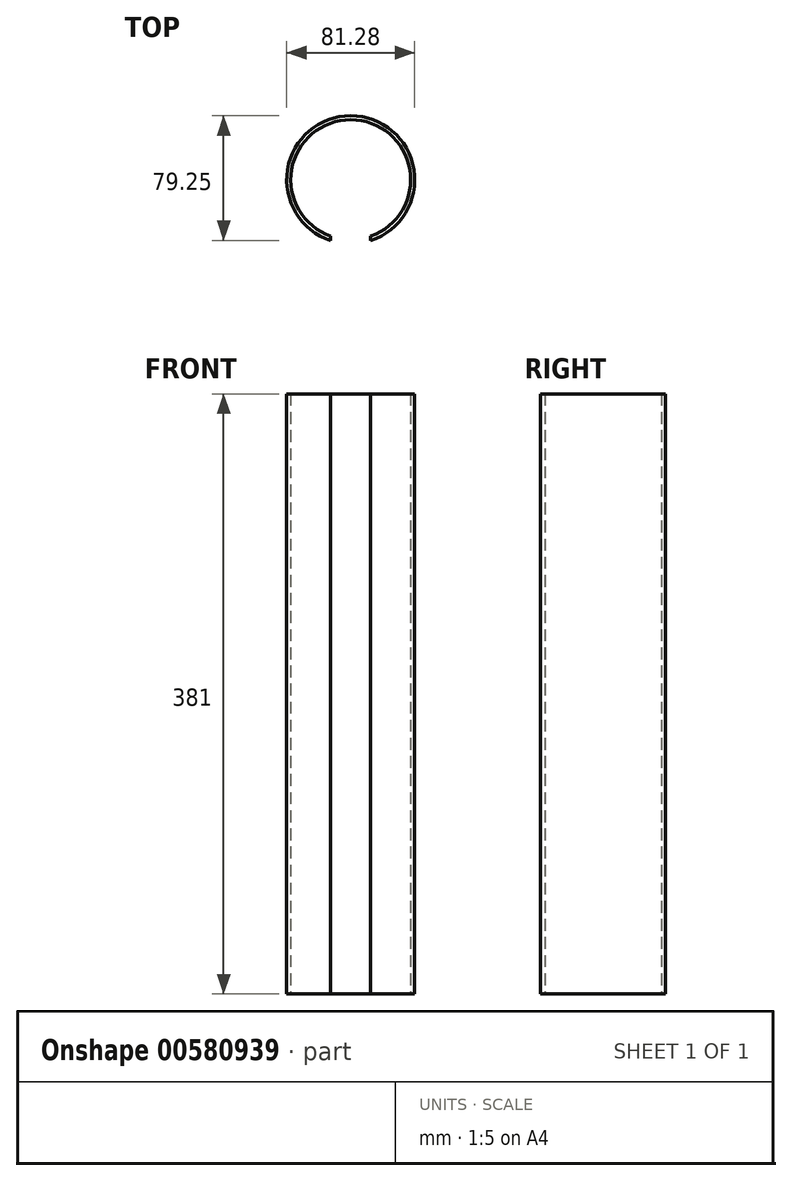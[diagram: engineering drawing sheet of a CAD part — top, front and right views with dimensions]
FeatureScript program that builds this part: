
annotation { "Feature Type Name" : "Feature", "Feature Type Description" : "" }
export const myFeature = defineFeature(function(context is Context, id is Id, definition is map)
    precondition{}
    {
        {
            var Q0;
            Q0=qCreatedBy(makeId("Top.planeOp"),FACE);
            var sketch = newSketch(context, id + "F0", { "sketchPlane" : qUnion([Q0])});
            skArc(sketch, "E0", {"start": v(8.75, -20.74) * mm, "mid": v(-3.95, 58.5) * mm, "end": v(-16.65, -20.74) * mm});
            skArc(sketch, "E1", {"start": v(8.75, -18.06) * mm, "mid": v(-3.95, 55.97) * mm, "end": v(-16.65, -18.06) * mm});
            skLineSegment(sketch, "E2", {"start": v(-16.65, -20.74) * mm, "end": v(-16.65, -18.06) * mm});
            skLineSegment(sketch, "E3", {"start": v(8.75, -20.74) * mm, "end": v(8.75, -18.06) * mm});
            skSolve(sketch);
        }
        {
            var Q0;
            Q0=makeQuery(id+"F0.imprint","IMPRINT",FACE,{"disambiguationData":[TD([[makeQuery(id+"F0.imprint","IMPRINT",EDGE,{"derivedFrom":sQuery(id+"F0.wireOp",EDGE,"E0")}),1.0]])]});
            extrude(context, id + "F1", {"entities" : qUnion([Q0]), "depth" : 381 * mm, "offsetDistance" : 25.4 * mm});
        }
    });
